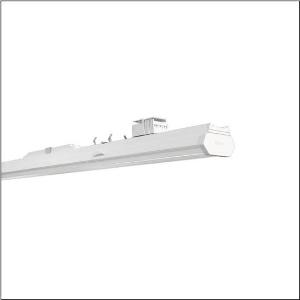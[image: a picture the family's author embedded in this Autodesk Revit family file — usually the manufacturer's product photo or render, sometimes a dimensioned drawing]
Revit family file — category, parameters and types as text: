
# Revit family: licross_11_protected_ho_51td12cn4exm
name_source: partatom
category: Lighting Fixtures
units: mm (PartAtom-declared; Revit-internal decimal feet)

## family parameters
Cut with Voids When Loaded = No
Host = Face
Light Source = No
Part Type = Normal
Room Calculation Point = No
Round Connector Dimension = Use Diameter
Shared = No

## types (1)
- --- (1 x LED, 14240 lm, 77.6 W, 4000K)
    Apparent Load = 78 VA
    CIE Flux Codes = 70 91 97 98 100
    Color Rendering = 80
    Color Temperature = 4000K
    Default Elevation = 1800 mm
    Description = Licross 11 Protected HO, luminaire insert, of sheet steel, galvanised, coil coated, white, length: 1.500mm, width: 90mm, height: 101mm, LED rated luminous flux: 14.240lm, light colour: 840, SDCM (Standard Deviation of Colour Matching)MacAdam ≤ 2 SDCM (initial), control gear: ON/OFF Multilumen, CLOi, with plug, 3-pole, with phase selection, mains connection: 220..240V, AC, 50/60Hz, start of lifetime: 78W, end of service life: 87W, internal wiring halogen-free, primary light control with lens, of plastic, primary optical cover: cover, of PMMA, light emission: direct distribution, primary light characteristic: symmetric, protection rating (complete): IP54, insulation class (complete): insulation class I (protective earthing), certification: CE, ENEC, VDE, UKCA, protection symbol: D if used in an environment with non-conductive dust loads with corresponding accessories, impact resistance: IK06, permissible ambient temperature for indoor applications: -35..+35°C, corresponds to IFS (International Featured Standards) requirements for safety and quality in the food industry, reducing of maximum allowable ambient temperature of 5°C with ceiling mounting, LABS conformity tested according to VDMA 24364:2018-05, The light source and the operating device comply with the requirements of the Ecodesign Regulation (EU) 2019/2020 and are replaceable in accordance with this regulation, packaging unit: 1 piece
    Height = 92 mm
    Lamp = 1 x LED
    Lamp Light Flux = 14240 lm
    Lamp Power = 77.6 W
    Lamp count = 1
    Length = 1500 mm
    Luminous efficacy = 184 lm/W
    Manufacturer = Siteco
    ModVariant = No
    Model = 51TD12CN4EXM
    Mounting Place = Ceiling
    Mounting Type = Pendant
    Number of Poles = 1
    OnlyDefault = Yes
    Power Factor = 1
    Product Name = Licross 11 Protected HO
    Product group = luminaire insert | ceiling pendant
    ProductGroupID = 901
    Protection Class = Protection class I
    Protection Degree = IP 54
    RLX_Detail_Level = 1
    RLX_Emergency_Light_Flux = 0 lm
    RLX_Emergency_Type = 0
    RLX_Emergency_Type_DB = No
    RlxData = <blob elided: 22437 chars, md5=c94c9874>
    Socket = socket
    Standby Power = 0 W
    System Light Flux = 14240 lm
    System Power = 78 W
    Type Comments = factory setting: luminous flux: 100 % | (A | C | E) | 181 mA
    Type Image = l_1256145.jpg
    URL = http://relux.com
    VarID = @adj_000935
    Voltage = 0 V
    Weight = 0.00 kg
    Width = 88 mm

## geometry (parser evidence)
native form markers: Blend x4, Sweep x12
no freeform markers — native parametric forms only
